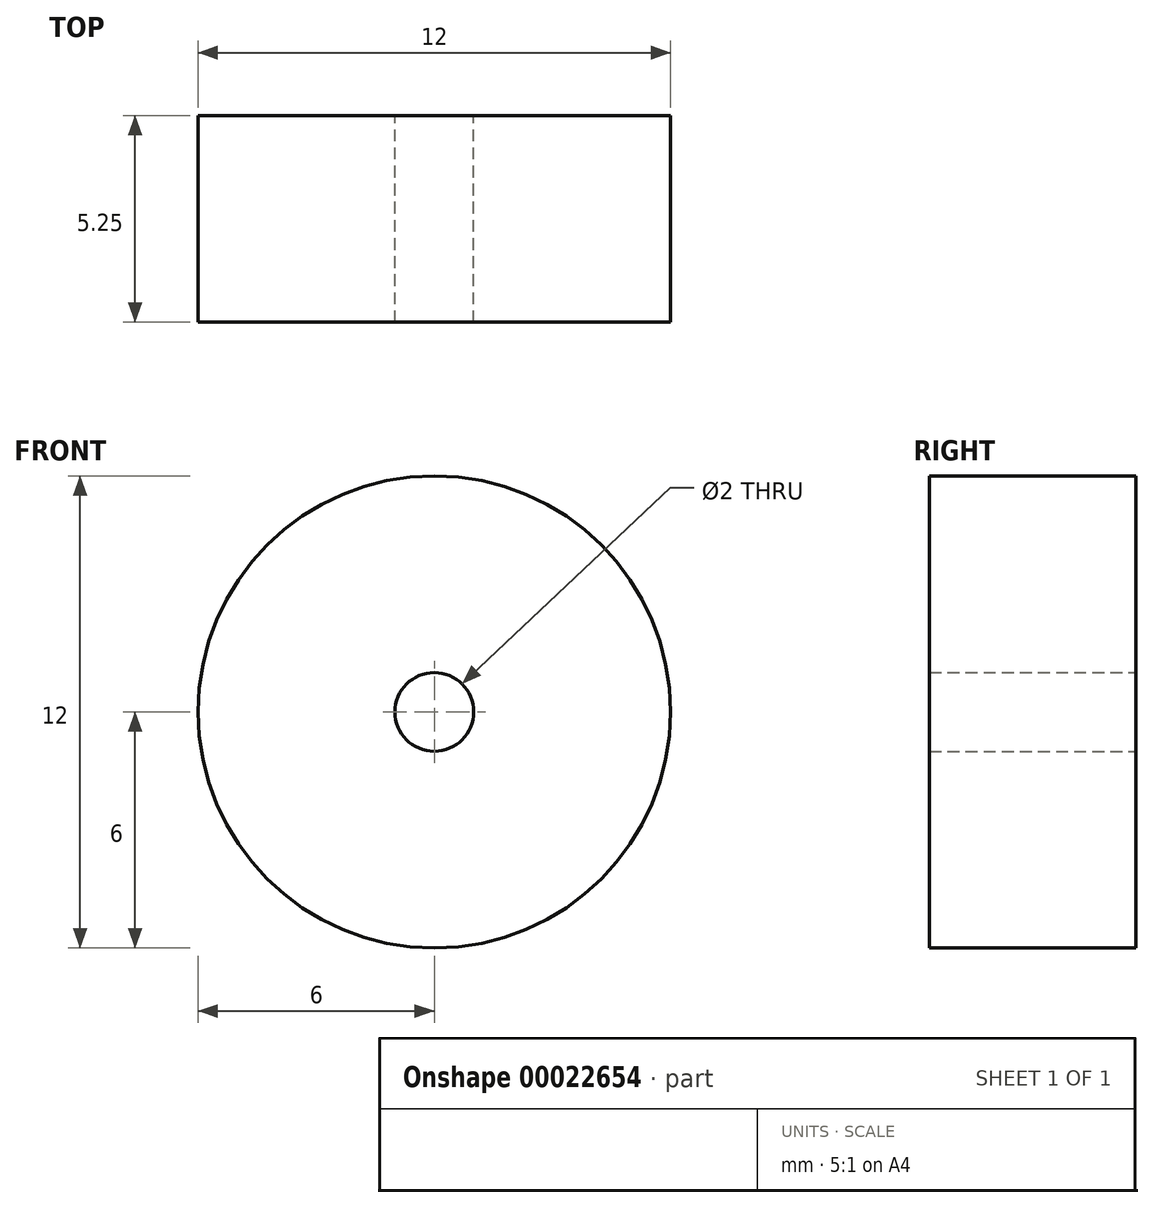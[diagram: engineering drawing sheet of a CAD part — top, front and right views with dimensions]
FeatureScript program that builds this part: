
annotation { "Feature Type Name" : "Feature", "Feature Type Description" : "" }
export const myFeature = defineFeature(function(context is Context, id is Id, definition is map)
    precondition{}
    {
        {
            var Q0;
            Q0=qCreatedBy(makeId("Front.planeOp"),FACE);
            var sketch = newSketch(context, id + "F0", { "sketchPlane" : qUnion([Q0])});
            skCircle(sketch, "E0", {"center": v(0, 0) * mm, "radius": 6 * mm});
            skCircle(sketch, "E1", {"center": v(0, 0) * mm, "radius": 1 * mm});
            skSolve(sketch);
        }
        {
            var Q0;
            Q0=makeQuery(id+"F0.imprint","IMPRINT",FACE,{"disambiguationData":[TD([[makeQuery(id+"F0.imprint","IMPRINT",EDGE,{"derivedFrom":sQuery(id+"F0.wireOp",EDGE,"E0")}),1.0]])]});
            extrude(context, id + "F1", {"entities" : qUnion([Q0]), "depth" : 5.25 * mm});
        }
    });
